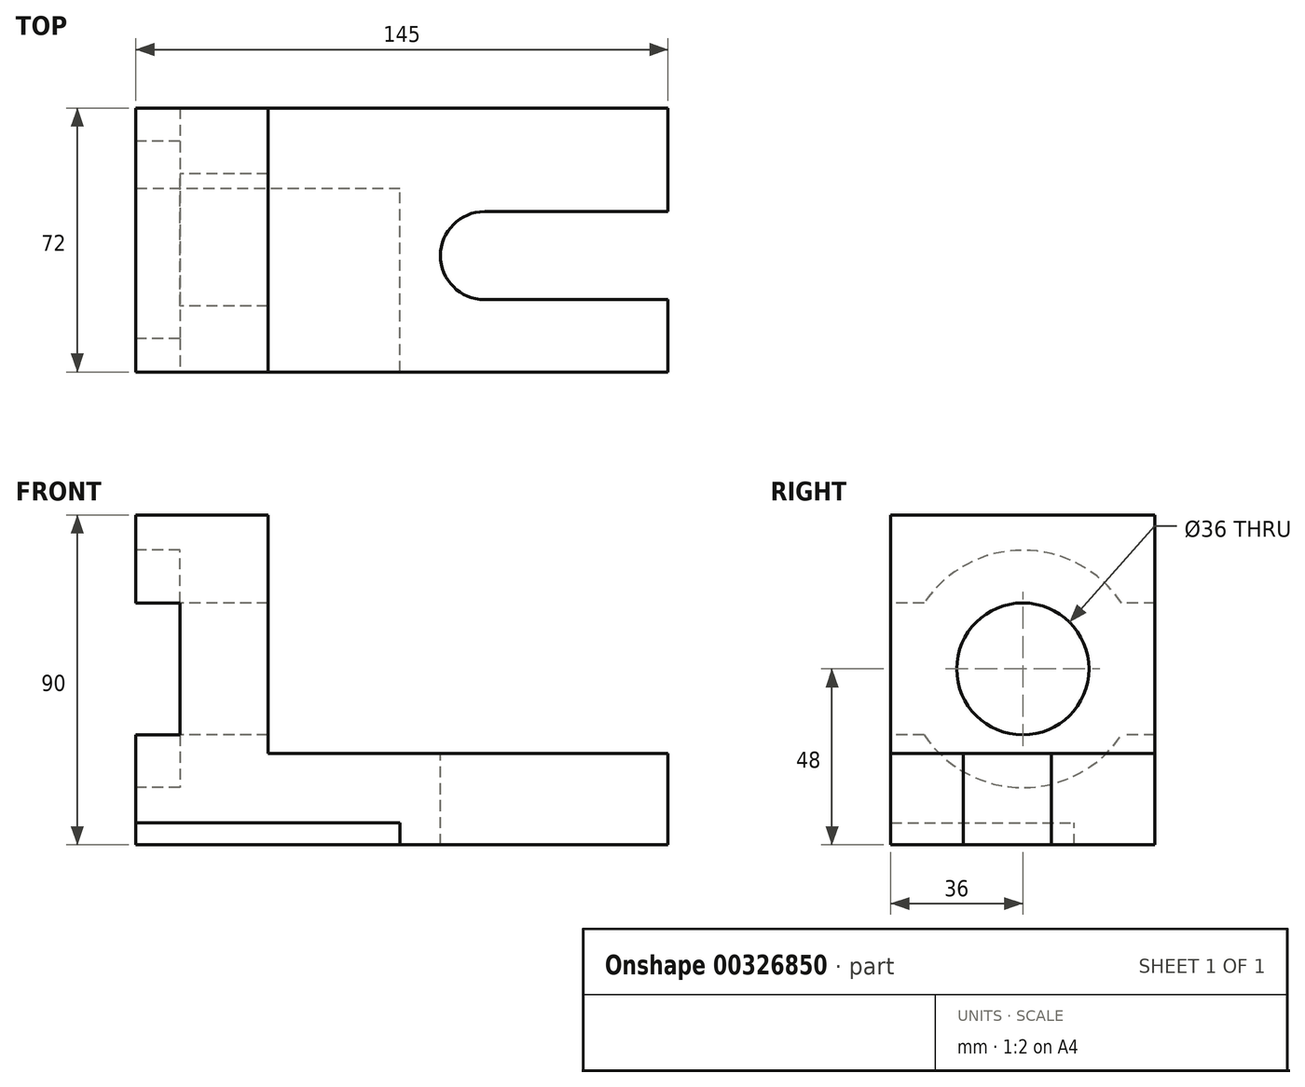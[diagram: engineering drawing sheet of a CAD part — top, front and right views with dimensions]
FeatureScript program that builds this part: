
annotation { "Feature Type Name" : "Feature", "Feature Type Description" : "" }
export const myFeature = defineFeature(function(context is Context, id is Id, definition is map)
    precondition{}
    {
        {
            var Q0;
            Q0=qCreatedBy(makeId("Top.planeOp"),FACE);
            var sketch = newSketch(context, id + "F0", { "sketchPlane" : qUnion([Q0])});
            skLineSegment(sketch, "E0.bottom", {"start": v(0, 0) * mm, "end": v(-145, 0) * mm});
            skLineSegment(sketch, "E0.top", {"start": v(0, 72) * mm, "end": v(-145, 72) * mm});
            skLineSegment(sketch, "E0.left", {"start": v(0, 0) * mm, "end": v(0, 72) * mm});
            skLineSegment(sketch, "E0.right", {"start": v(-145, 0) * mm, "end": v(-145, 72) * mm});
            skSolve(sketch);
        }
        {
            var Q0;
            Q0=makeQuery(id+"F0.imprint","IMPRINT",FACE,{"disambiguationData":[TD([[makeQuery(id+"F0.imprint","IMPRINT",EDGE,{"derivedFrom":sQuery(id+"F0.wireOp",EDGE,"E0.bottom")}),-1.0]])]});
            extrude(context, id + "F1", {"entities" : qUnion([Q0]), "depth" : 90 * mm});
        }
        {
            var Q0;
            Q0=makeQuery(id+"F1.opExtrude","SWEPT_FACE",FACE,{"disambiguationData":[OSD([sQuery(id+"F0.wireOp",EDGE,"E0.bottom")])]});
            var sketch = newSketch(context, id + "F2", { "sketchPlane" : qUnion([Q0])});
            skLineSegment(sketch, "E1.bottom", {"start": v(0, 90) * mm, "end": v(-109, 90) * mm});
            skLineSegment(sketch, "E1.top", {"start": v(0, 25) * mm, "end": v(-109, 25) * mm});
            skLineSegment(sketch, "E1.left", {"start": v(0, 90) * mm, "end": v(0, 25) * mm});
            skLineSegment(sketch, "E1.right", {"start": v(-109, 90) * mm, "end": v(-109, 25) * mm});
            skSolve(sketch);
        }
        {
            var Q0;
            Q0=makeQuery(id+"F2.imprint","IMPRINT",FACE,{"disambiguationData":[TD([[makeQuery(id+"F2.imprint","IMPRINT",EDGE,{"derivedFrom":sQuery(id+"F2.wireOp",EDGE,"E1.bottom")}),1.0]])]});
            extrude(context, id + "F3", {"entities" : qUnion([Q0]), "operationType" : NewBodyOperationType.REMOVE, "oppositeDirection" : true, "depth" : 90 * mm});
        }
        {
            var Q0;
            Q0=makeQuery(id+"F3.boolean.opBoolean","COPY",FACE,{"derivedFrom":makeQuery(id+"F3.opExtrude","SWEPT_FACE",FACE,{"disambiguationData":[OSD([sQuery(id+"F2.wireOp",EDGE,"E1.top")])]})});
            var sketch = newSketch(context, id + "F4", { "sketchPlane" : qUnion([Q0])});
            skLineSegment(sketch, "E2.bottom", {"start": v(0, 19.74) * mm, "end": v(-50, 19.74) * mm});
            skLineSegment(sketch, "E2.top", {"start": v(0, 43.74) * mm, "end": v(-50, 43.74) * mm});
            skLineSegment(sketch, "E2.left", {"start": v(0, 19.74) * mm, "end": v(0, 43.74) * mm});
            skArc(sketch, "E3", {"start": v(-50, 43.74) * mm, "mid": v(-62, 31.74) * mm, "end": v(-50, 19.74) * mm});
            skSolve(sketch);
        }
        {
            var Q0;
            Q0=makeQuery(id+"F4.imprint","IMPRINT",FACE,{"disambiguationData":[TD([[makeQuery(id+"F4.imprint","IMPRINT",EDGE,{"derivedFrom":sQuery(id+"F4.wireOp",EDGE,"E2.bottom")}),-1.0]])]});
            extrude(context, id + "F5", {"entities" : qUnion([Q0]), "operationType" : NewBodyOperationType.REMOVE, "oppositeDirection" : true, "depth" : 25.4 * mm});
        }
        {
            var Q0;
            Q0=makeQuery(id+"F1.opExtrude","SWEPT_FACE",FACE,{"disambiguationData":[OSD([sQuery(id+"F0.wireOp",EDGE,"E0.right")])]});
            var sketch = newSketch(context, id + "F6", { "sketchPlane" : qUnion([Q0])});
            skLineSegment(sketch, "E4.bottom", {"start": v(0, 0) * mm, "end": v(-50, 0) * mm});
            skLineSegment(sketch, "E4.top", {"start": v(0, 6) * mm, "end": v(-50, 6) * mm});
            skLineSegment(sketch, "E4.left", {"start": v(0, 0) * mm, "end": v(0, 6) * mm});
            skLineSegment(sketch, "E4.right", {"start": v(-50, 0) * mm, "end": v(-50, 6) * mm});
            skSolve(sketch);
        }
        {
            var Q0;
            Q0=makeQuery(id+"F6.imprint","IMPRINT",FACE,{"disambiguationData":[TD([[makeQuery(id+"F6.imprint","IMPRINT",EDGE,{"derivedFrom":sQuery(id+"F6.wireOp",EDGE,"E4.bottom")}),-1.0]])]});
            extrude(context, id + "F7", {"entities" : qUnion([Q0]), "operationType" : NewBodyOperationType.REMOVE, "oppositeDirection" : true, "depth" : 72 * mm});
        }
        {
            var Q0;
            Q0=makeQuery(id+"F1.opExtrude","SWEPT_FACE",FACE,{"disambiguationData":[OSD([sQuery(id+"F0.wireOp",EDGE,"E0.right")])]});
            var sketch = newSketch(context, id + "F8", { "sketchPlane" : qUnion([Q0])});
            skCircle(sketch, "E5", {"center": v(-36, 48) * mm, "radius": 32.38 * mm});
            skPoint(sketch, "E5.centerSnap0", {"position": v(-36, 90) * mm});
            skPoint(sketch, "E5.centerSnap1", {"position": v(0, 48) * mm});
            skLineSegment(sketch, "E6.bottom", {"start": v(-86.05, 66) * mm, "end": v(23.42, 66) * mm});
            skLineSegment(sketch, "E6.top", {"start": v(-86.05, 30) * mm, "end": v(23.42, 30) * mm});
            skSolve(sketch);
        }
        {
            var Q0;
            {var subQ0=sQuery(id+"F8.wireOp",EDGE,"E6.bottom");var subQ1=sQuery(id+"F8.wireOp",EDGE,"E5");var subQ2=makeQuery(id+"F8.imprint","INTERSECT",VERTEX,{"disambiguationData":[OD(0.0)],"derivedFrom":[subQ1,subQ0]});Q0=makeQuery(id+"F8.imprint","IMPRINT",FACE,{"disambiguationData":[TD([[makeQuery(id+"F8.imprint","IMPRINT",EDGE,{"disambiguationData":[TD([[subQ2,-1.0]])],"derivedFrom":subQ1}),-1.0]])]});}
            var Q1;
            {var subQ0=sQuery(id+"F8.wireOp",EDGE,"E6.bottom");var subQ1=sQuery(id+"F8.wireOp",EDGE,"E5");var subQ2=makeQuery(id+"F8.imprint","INTERSECT",VERTEX,{"disambiguationData":[OD(0.0)],"derivedFrom":[subQ1,subQ0]});Q1=makeQuery(id+"F8.imprint","IMPRINT",FACE,{"disambiguationData":[TD([[makeQuery(id+"F8.imprint","IMPRINT",EDGE,{"disambiguationData":[TD([[subQ2,1.0]])],"derivedFrom":subQ1}),1.0]])]});}
            var Q2;
            {var subQ0=sQuery(id+"F8.wireOp",EDGE,"E6.bottom");var subQ1=sQuery(id+"F8.wireOp",EDGE,"E5");var subQ2=makeQuery(id+"F8.imprint","INTERSECT",VERTEX,{"disambiguationData":[OD(1.0)],"derivedFrom":[subQ1,subQ0]});Q2=makeQuery(id+"F8.imprint","IMPRINT",FACE,{"disambiguationData":[TD([[makeQuery(id+"F8.imprint","IMPRINT",EDGE,{"disambiguationData":[TD([[subQ2,1.0]])],"derivedFrom":subQ1}),-1.0]])]});}
            var Q3;
            {var subQ0=sQuery(id+"F8.wireOp",EDGE,"E6.top");var subQ1=sQuery(id+"F8.wireOp",EDGE,"E5");var subQ2=makeQuery(id+"F8.imprint","INTERSECT",VERTEX,{"disambiguationData":[OD(0.0)],"derivedFrom":[subQ1,subQ0]});Q3=makeQuery(id+"F8.imprint","IMPRINT",FACE,{"disambiguationData":[TD([[makeQuery(id+"F8.imprint","IMPRINT",EDGE,{"disambiguationData":[TD([[subQ2,-1.0]])],"derivedFrom":subQ1}),1.0]])]});}
            var Q4;
            {var subQ0=sQuery(id+"F8.wireOp",EDGE,"E6.bottom");var subQ1=sQuery(id+"F8.wireOp",EDGE,"E5");var subQ2=makeQuery(id+"F8.imprint","INTERSECT",VERTEX,{"disambiguationData":[OD(0.0)],"derivedFrom":[subQ1,subQ0]});Q4=makeQuery(id+"F8.imprint","IMPRINT",FACE,{"disambiguationData":[TD([[makeQuery(id+"F8.imprint","IMPRINT",EDGE,{"disambiguationData":[TD([[subQ2,-1.0]])],"derivedFrom":subQ1}),1.0]])]});}
            extrude(context, id + "F9", {"entities" : qUnion([Q0, Q1, Q2, Q3, Q4]), "operationType" : NewBodyOperationType.REMOVE, "oppositeDirection" : true, "depth" : 12 * mm});
        }
        {
            var Q0;
            Q0=makeQuery(id+"F9.boolean.opBoolean","COPY",FACE,{"derivedFrom":makeQuery(id+"F9.opExtrude","CAP_FACE",FACE,{"disambiguationData":[OSD([sQuery(id+"F0.wireOp",EDGE,"E0.bottom"),sQuery(id+"F0.wireOp",EDGE,"E0.top"),sQuery(id+"F0.wireOp",EDGE,"E0.right"),sQuery(id+"F8.wireOp",EDGE,"E5"),sQuery(id+"F8.wireOp",EDGE,"E6.bottom"),sQuery(id+"F8.wireOp",EDGE,"E6.top")])],"isStart":false})});
            var sketch = newSketch(context, id + "F10", { "sketchPlane" : qUnion([Q0])});
            skCircle(sketch, "E7", {"center": v(-36, 48) * mm, "radius": 18 * mm});
            skSolve(sketch);
        }
        {
            var Q0;
            Q0=makeQuery(id+"F10.imprint","IMPRINT",FACE,{"disambiguationData":[TD([[makeQuery(id+"F10.imprint","IMPRINT",EDGE,{"derivedFrom":sQuery(id+"F10.wireOp",EDGE,"E7")}),1.0]])]});
            extrude(context, id + "F11", {"entities" : qUnion([Q0]), "operationType" : NewBodyOperationType.REMOVE, "endBound" : BoundingType.UP_TO_NEXT, "oppositeDirection" : true, "depth" : 25.4 * mm});
        }
    });
